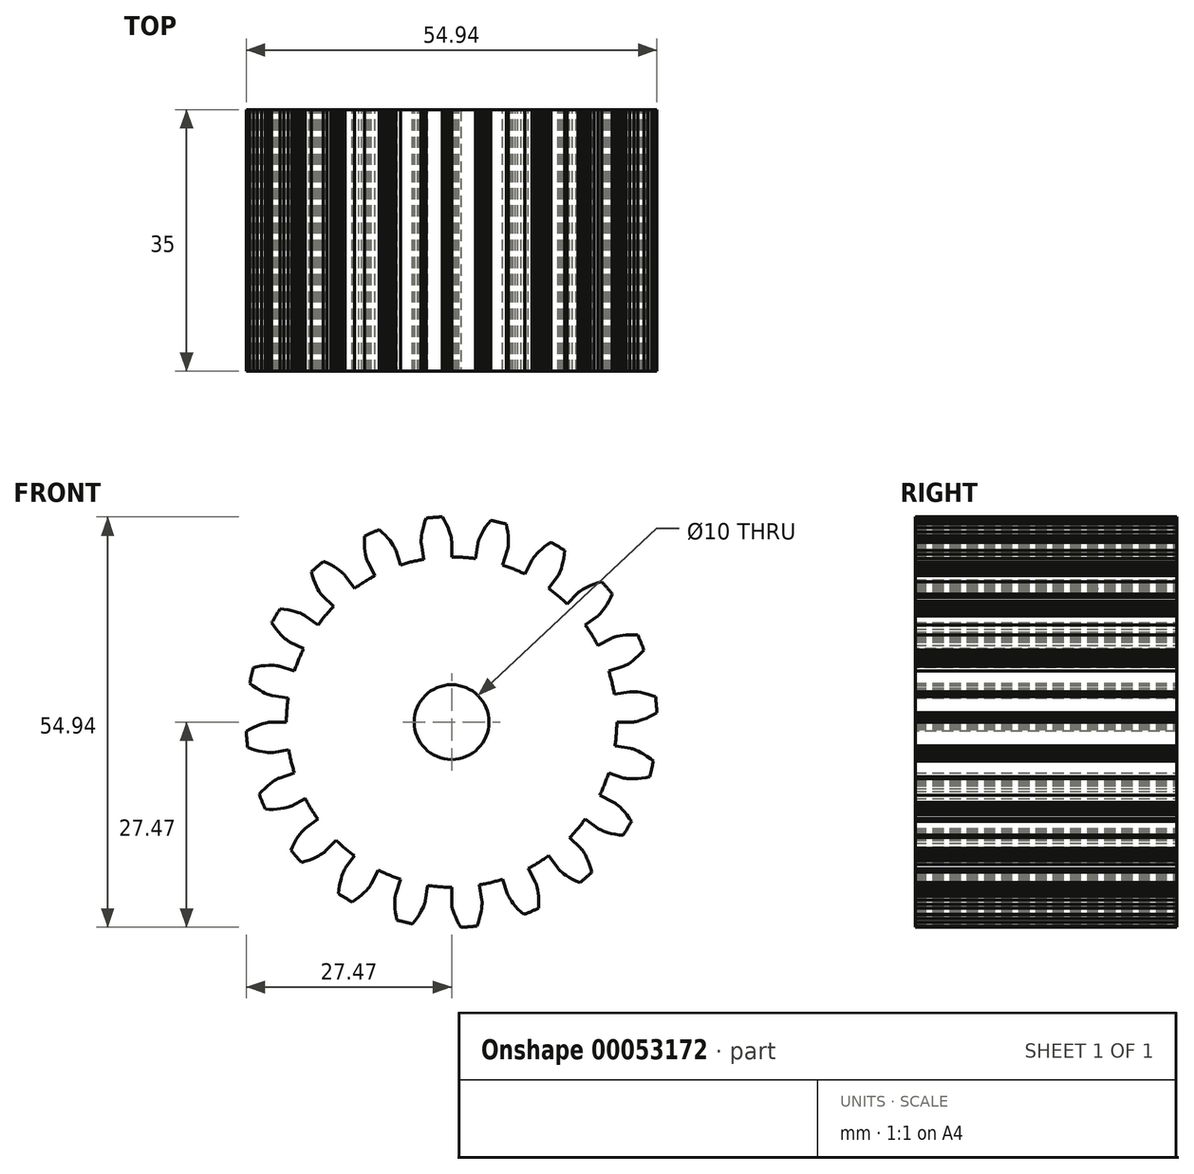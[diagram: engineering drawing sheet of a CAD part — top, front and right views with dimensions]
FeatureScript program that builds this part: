
annotation { "Feature Type Name" : "Feature", "Feature Type Description" : "" }
export const myFeature = defineFeature(function(context is Context, id is Id, definition is map)
    precondition{}
    {
        {
            var Q0;
            Q0=qCreatedBy(makeId("Front.planeOp"),FACE);
            var sketch = newSketch(context, id + "F0", { "sketchPlane" : qUnion([Q0])});
            skLineSegment(sketch, "E0", {"start": v(-24.2, 0) * mm, "end": v(-24.23, 0) * mm});
            skLineSegment(sketch, "E1", {"start": v(-24.23, 0) * mm, "end": v(-24.32, 0) * mm});
            skLineSegment(sketch, "E2", {"start": v(-24.32, 0) * mm, "end": v(-24.47, -0.03) * mm});
            skLineSegment(sketch, "E3", {"start": v(-24.47, -0.03) * mm, "end": v(-24.68, -0.06) * mm});
            skLineSegment(sketch, "E4", {"start": v(-24.68, -0.06) * mm, "end": v(-24.94, -0.13) * mm});
            skLineSegment(sketch, "E5", {"start": v(-24.94, -0.13) * mm, "end": v(-25.26, -0.22) * mm});
            skLineSegment(sketch, "E6", {"start": v(-25.26, -0.22) * mm, "end": v(-25.64, -0.34) * mm});
            skLineSegment(sketch, "E7", {"start": v(-25.64, -0.34) * mm, "end": v(-26.06, -0.5) * mm});
            skLineSegment(sketch, "E8", {"start": v(-26.06, -0.5) * mm, "end": v(-26.53, -0.72) * mm});
            skLineSegment(sketch, "E9", {"start": v(-26.53, -0.72) * mm, "end": v(-27.04, -0.98) * mm});
            skLineSegment(sketch, "E10", {"start": v(-27.04, -0.98) * mm, "end": v(-27.47, -1.24) * mm});
            skLineSegment(sketch, "E11", {"start": v(-23.86, -4.06) * mm, "end": v(-23.89, -4.06) * mm});
            skLineSegment(sketch, "E12", {"start": v(-23.89, -4.06) * mm, "end": v(-23.98, -4.07) * mm});
            skLineSegment(sketch, "E13", {"start": v(-23.98, -4.07) * mm, "end": v(-24.13, -4.07) * mm});
            skLineSegment(sketch, "E14", {"start": v(-24.13, -4.07) * mm, "end": v(-24.34, -4.07) * mm});
            skLineSegment(sketch, "E15", {"start": v(-24.34, -4.07) * mm, "end": v(-24.61, -4.06) * mm});
            skLineSegment(sketch, "E16", {"start": v(-24.61, -4.06) * mm, "end": v(-24.94, -4.02) * mm});
            skLineSegment(sketch, "E17", {"start": v(-24.94, -4.02) * mm, "end": v(-25.33, -3.96) * mm});
            skLineSegment(sketch, "E18", {"start": v(-25.33, -3.96) * mm, "end": v(-25.78, -3.87) * mm});
            skLineSegment(sketch, "E19", {"start": v(-25.78, -3.87) * mm, "end": v(-26.27, -3.73) * mm});
            skLineSegment(sketch, "E20", {"start": v(-26.27, -3.73) * mm, "end": v(-26.82, -3.56) * mm});
            skLineSegment(sketch, "E21", {"start": v(-26.82, -3.56) * mm, "end": v(-27.3, -3.39) * mm});
            skLineSegment(sketch, "E22", {"start": v(-23.86, -4.06) * mm, "end": v(-21.8, -3.7) * mm});
            skLineSegment(sketch, "E23", {"start": v(-24.2, 0) * mm, "end": v(-22.1, 0) * mm});
            skArc(sketch, "E24", {"start": v(-27.47, -1.24) * mm, "mid": v(-27.4, -2.31) * mm, "end": v(-27.3, -3.39) * mm});
            skLineSegment(sketch, "E25", {"start": v(-23.02, -7.48) * mm, "end": v(-23.04, -7.49) * mm});
            skLineSegment(sketch, "E26", {"start": v(-23.04, -7.49) * mm, "end": v(-23.13, -7.52) * mm});
            skLineSegment(sketch, "E27", {"start": v(-23.13, -7.52) * mm, "end": v(-23.26, -7.59) * mm});
            skLineSegment(sketch, "E28", {"start": v(-23.26, -7.59) * mm, "end": v(-23.45, -7.69) * mm});
            skLineSegment(sketch, "E29", {"start": v(-23.45, -7.69) * mm, "end": v(-23.68, -7.83) * mm});
            skLineSegment(sketch, "E30", {"start": v(-23.68, -7.83) * mm, "end": v(-23.96, -8.01) * mm});
            skLineSegment(sketch, "E31", {"start": v(-23.96, -8.01) * mm, "end": v(-24.28, -8.25) * mm});
            skLineSegment(sketch, "E32", {"start": v(-24.28, -8.25) * mm, "end": v(-24.63, -8.54) * mm});
            skLineSegment(sketch, "E33", {"start": v(-24.63, -8.54) * mm, "end": v(-25, -8.88) * mm});
            skLineSegment(sketch, "E34", {"start": v(-25, -8.88) * mm, "end": v(-25.41, -9.3) * mm});
            skLineSegment(sketch, "E35", {"start": v(-25.41, -9.3) * mm, "end": v(-25.75, -9.66) * mm});
            skLineSegment(sketch, "E36", {"start": v(-21.44, -11.23) * mm, "end": v(-21.46, -11.24) * mm});
            skLineSegment(sketch, "E37", {"start": v(-21.46, -11.24) * mm, "end": v(-21.55, -11.28) * mm});
            skLineSegment(sketch, "E38", {"start": v(-21.55, -11.28) * mm, "end": v(-21.69, -11.33) * mm});
            skLineSegment(sketch, "E39", {"start": v(-21.69, -11.33) * mm, "end": v(-21.9, -11.4) * mm});
            skLineSegment(sketch, "E40", {"start": v(-21.9, -11.4) * mm, "end": v(-22.15, -11.46) * mm});
            skLineSegment(sketch, "E41", {"start": v(-22.15, -11.46) * mm, "end": v(-22.48, -11.53) * mm});
            skLineSegment(sketch, "E42", {"start": v(-22.48, -11.53) * mm, "end": v(-22.87, -11.6) * mm});
            skLineSegment(sketch, "E43", {"start": v(-22.87, -11.6) * mm, "end": v(-23.32, -11.64) * mm});
            skLineSegment(sketch, "E44", {"start": v(-23.32, -11.64) * mm, "end": v(-23.83, -11.67) * mm});
            skLineSegment(sketch, "E45", {"start": v(-23.83, -11.67) * mm, "end": v(-24.4, -11.67) * mm});
            skLineSegment(sketch, "E46", {"start": v(-24.4, -11.67) * mm, "end": v(-24.9, -11.65) * mm});
            skLineSegment(sketch, "E47", {"start": v(-21.44, -11.23) * mm, "end": v(-19.58, -10.26) * mm});
            skLineSegment(sketch, "E48", {"start": v(-23.02, -7.48) * mm, "end": v(-21.03, -6.83) * mm});
            skArc(sketch, "E49", {"start": v(-25.75, -9.66) * mm, "mid": v(-25.35, -10.67) * mm, "end": v(-24.9, -11.65) * mm});
            skLineSegment(sketch, "E50", {"start": v(-19.58, -14.22) * mm, "end": v(-19.6, -14.24) * mm});
            skLineSegment(sketch, "E51", {"start": v(-19.6, -14.24) * mm, "end": v(-19.67, -14.3) * mm});
            skLineSegment(sketch, "E52", {"start": v(-19.67, -14.3) * mm, "end": v(-19.78, -14.4) * mm});
            skLineSegment(sketch, "E53", {"start": v(-19.78, -14.4) * mm, "end": v(-19.93, -14.56) * mm});
            skLineSegment(sketch, "E54", {"start": v(-19.93, -14.56) * mm, "end": v(-20.1, -14.76) * mm});
            skLineSegment(sketch, "E55", {"start": v(-20.1, -14.76) * mm, "end": v(-20.31, -15.03) * mm});
            skLineSegment(sketch, "E56", {"start": v(-20.31, -15.03) * mm, "end": v(-20.54, -15.35) * mm});
            skLineSegment(sketch, "E57", {"start": v(-20.54, -15.35) * mm, "end": v(-20.78, -15.73) * mm});
            skLineSegment(sketch, "E58", {"start": v(-20.78, -15.73) * mm, "end": v(-21.04, -16.18) * mm});
            skLineSegment(sketch, "E59", {"start": v(-21.04, -16.18) * mm, "end": v(-21.3, -16.69) * mm});
            skLineSegment(sketch, "E60", {"start": v(-21.3, -16.69) * mm, "end": v(-21.5, -17.15) * mm});
            skLineSegment(sketch, "E61", {"start": v(-16.92, -17.3) * mm, "end": v(-16.94, -17.33) * mm});
            skLineSegment(sketch, "E62", {"start": v(-16.94, -17.33) * mm, "end": v(-17, -17.38) * mm});
            skLineSegment(sketch, "E63", {"start": v(-17, -17.38) * mm, "end": v(-17.13, -17.48) * mm});
            skLineSegment(sketch, "E64", {"start": v(-17.13, -17.48) * mm, "end": v(-17.3, -17.6) * mm});
            skLineSegment(sketch, "E65", {"start": v(-17.3, -17.6) * mm, "end": v(-17.53, -17.75) * mm});
            skLineSegment(sketch, "E66", {"start": v(-17.53, -17.75) * mm, "end": v(-17.82, -17.91) * mm});
            skLineSegment(sketch, "E67", {"start": v(-17.82, -17.91) * mm, "end": v(-18.17, -18.1) * mm});
            skLineSegment(sketch, "E68", {"start": v(-18.17, -18.1) * mm, "end": v(-18.58, -18.28) * mm});
            skLineSegment(sketch, "E69", {"start": v(-18.58, -18.28) * mm, "end": v(-19.06, -18.46) * mm});
            skLineSegment(sketch, "E70", {"start": v(-19.06, -18.46) * mm, "end": v(-19.6, -18.65) * mm});
            skLineSegment(sketch, "E71", {"start": v(-19.6, -18.65) * mm, "end": v(-20.09, -18.78) * mm});
            skLineSegment(sketch, "E72", {"start": v(-16.92, -17.3) * mm, "end": v(-15.45, -15.8) * mm});
            skLineSegment(sketch, "E73", {"start": v(-19.58, -14.22) * mm, "end": v(-17.89, -13) * mm});
            skArc(sketch, "E74", {"start": v(-21.5, -17.15) * mm, "mid": v(-20.8, -17.98) * mm, "end": v(-20.09, -18.78) * mm});
            skLineSegment(sketch, "E75", {"start": v(-14.22, -19.58) * mm, "end": v(-14.24, -19.6) * mm});
            skLineSegment(sketch, "E76", {"start": v(-14.24, -19.6) * mm, "end": v(-14.29, -19.68) * mm});
            skLineSegment(sketch, "E77", {"start": v(-14.29, -19.68) * mm, "end": v(-14.36, -19.81) * mm});
            skLineSegment(sketch, "E78", {"start": v(-14.36, -19.81) * mm, "end": v(-14.45, -20) * mm});
            skLineSegment(sketch, "E79", {"start": v(-14.45, -20) * mm, "end": v(-14.56, -20.25) * mm});
            skLineSegment(sketch, "E80", {"start": v(-14.56, -20.25) * mm, "end": v(-14.68, -20.57) * mm});
            skLineSegment(sketch, "E81", {"start": v(-14.68, -20.57) * mm, "end": v(-14.8, -20.94) * mm});
            skLineSegment(sketch, "E82", {"start": v(-14.8, -20.94) * mm, "end": v(-14.9, -21.38) * mm});
            skLineSegment(sketch, "E83", {"start": v(-14.9, -21.38) * mm, "end": v(-15, -21.89) * mm});
            skLineSegment(sketch, "E84", {"start": v(-15, -21.89) * mm, "end": v(-15.1, -22.45) * mm});
            skLineSegment(sketch, "E85", {"start": v(-15.1, -22.45) * mm, "end": v(-15.15, -22.95) * mm});
            skLineSegment(sketch, "E86", {"start": v(-10.74, -21.69) * mm, "end": v(-10.76, -21.71) * mm});
            skLineSegment(sketch, "E87", {"start": v(-10.76, -21.71) * mm, "end": v(-10.8, -21.79) * mm});
            skLineSegment(sketch, "E88", {"start": v(-10.8, -21.79) * mm, "end": v(-10.89, -21.92) * mm});
            skLineSegment(sketch, "E89", {"start": v(-10.89, -21.92) * mm, "end": v(-11.01, -22.09) * mm});
            skLineSegment(sketch, "E90", {"start": v(-11.01, -22.09) * mm, "end": v(-11.19, -22.3) * mm});
            skLineSegment(sketch, "E91", {"start": v(-11.19, -22.3) * mm, "end": v(-11.4, -22.54) * mm});
            skLineSegment(sketch, "E92", {"start": v(-11.4, -22.54) * mm, "end": v(-11.69, -22.82) * mm});
            skLineSegment(sketch, "E93", {"start": v(-11.69, -22.82) * mm, "end": v(-12.02, -23.13) * mm});
            skLineSegment(sketch, "E94", {"start": v(-12.02, -23.13) * mm, "end": v(-12.42, -23.45) * mm});
            skLineSegment(sketch, "E95", {"start": v(-12.42, -23.45) * mm, "end": v(-12.88, -23.8) * mm});
            skLineSegment(sketch, "E96", {"start": v(-12.88, -23.8) * mm, "end": v(-13.3, -24.07) * mm});
            skLineSegment(sketch, "E97", {"start": v(-10.74, -21.69) * mm, "end": v(-9.81, -19.81) * mm});
            skLineSegment(sketch, "E98", {"start": v(-14.22, -19.58) * mm, "end": v(-13, -17.89) * mm});
            skArc(sketch, "E99", {"start": v(-15.15, -22.95) * mm, "mid": v(-14.24, -23.53) * mm, "end": v(-13.3, -24.07) * mm});
            skLineSegment(sketch, "E100", {"start": v(-7.48, -23.02) * mm, "end": v(-7.49, -23.04) * mm});
            skLineSegment(sketch, "E101", {"start": v(-7.49, -23.04) * mm, "end": v(-7.5, -23.13) * mm});
            skLineSegment(sketch, "E102", {"start": v(-7.5, -23.13) * mm, "end": v(-7.54, -23.28) * mm});
            skLineSegment(sketch, "E103", {"start": v(-7.54, -23.28) * mm, "end": v(-7.56, -23.5) * mm});
            skLineSegment(sketch, "E104", {"start": v(-7.56, -23.5) * mm, "end": v(-7.59, -23.76) * mm});
            skLineSegment(sketch, "E105", {"start": v(-7.59, -23.76) * mm, "end": v(-7.6, -24.1) * mm});
            skLineSegment(sketch, "E106", {"start": v(-7.6, -24.1) * mm, "end": v(-7.6, -24.49) * mm});
            skLineSegment(sketch, "E107", {"start": v(-7.6, -24.49) * mm, "end": v(-7.57, -24.94) * mm});
            skLineSegment(sketch, "E108", {"start": v(-7.57, -24.94) * mm, "end": v(-7.51, -25.45) * mm});
            skLineSegment(sketch, "E109", {"start": v(-7.51, -25.45) * mm, "end": v(-7.42, -26.02) * mm});
            skLineSegment(sketch, "E110", {"start": v(-7.42, -26.02) * mm, "end": v(-7.31, -26.5) * mm});
            skLineSegment(sketch, "E111", {"start": v(-3.52, -23.94) * mm, "end": v(-3.52, -23.97) * mm});
            skLineSegment(sketch, "E112", {"start": v(-3.52, -23.97) * mm, "end": v(-3.54, -24.06) * mm});
            skLineSegment(sketch, "E113", {"start": v(-3.54, -24.06) * mm, "end": v(-3.58, -24.2) * mm});
            skLineSegment(sketch, "E114", {"start": v(-3.58, -24.2) * mm, "end": v(-3.65, -24.4) * mm});
            skLineSegment(sketch, "E115", {"start": v(-3.65, -24.4) * mm, "end": v(-3.75, -24.66) * mm});
            skLineSegment(sketch, "E116", {"start": v(-3.75, -24.66) * mm, "end": v(-3.88, -24.97) * mm});
            skLineSegment(sketch, "E117", {"start": v(-3.88, -24.97) * mm, "end": v(-4.06, -25.32) * mm});
            skLineSegment(sketch, "E118", {"start": v(-4.06, -25.32) * mm, "end": v(-4.29, -25.7) * mm});
            skLineSegment(sketch, "E119", {"start": v(-4.29, -25.7) * mm, "end": v(-4.57, -26.14) * mm});
            skLineSegment(sketch, "E120", {"start": v(-4.57, -26.14) * mm, "end": v(-4.9, -26.6) * mm});
            skLineSegment(sketch, "E121", {"start": v(-4.9, -26.6) * mm, "end": v(-5.21, -27) * mm});
            skLineSegment(sketch, "E122", {"start": v(-3.52, -23.94) * mm, "end": v(-3.21, -21.87) * mm});
            skLineSegment(sketch, "E123", {"start": v(-7.48, -23.02) * mm, "end": v(-6.83, -21.03) * mm});
            skArc(sketch, "E124", {"start": v(-7.31, -26.5) * mm, "mid": v(-6.27, -26.78) * mm, "end": v(-5.21, -27) * mm});
            skLineSegment(sketch, "E125", {"start": v(0, -24.2) * mm, "end": v(0, -24.23) * mm});
            skLineSegment(sketch, "E126", {"start": v(0, -24.23) * mm, "end": v(0, -24.32) * mm});
            skLineSegment(sketch, "E127", {"start": v(0, -24.32) * mm, "end": v(0.03, -24.47) * mm});
            skLineSegment(sketch, "E128", {"start": v(0.03, -24.47) * mm, "end": v(0.06, -24.68) * mm});
            skLineSegment(sketch, "E129", {"start": v(0.06, -24.68) * mm, "end": v(0.13, -24.94) * mm});
            skLineSegment(sketch, "E130", {"start": v(0.13, -24.94) * mm, "end": v(0.22, -25.26) * mm});
            skLineSegment(sketch, "E131", {"start": v(0.22, -25.26) * mm, "end": v(0.34, -25.64) * mm});
            skLineSegment(sketch, "E132", {"start": v(0.34, -25.64) * mm, "end": v(0.5, -26.06) * mm});
            skLineSegment(sketch, "E133", {"start": v(0.5, -26.06) * mm, "end": v(0.72, -26.53) * mm});
            skLineSegment(sketch, "E134", {"start": v(0.72, -26.53) * mm, "end": v(0.98, -27.04) * mm});
            skLineSegment(sketch, "E135", {"start": v(0.98, -27.04) * mm, "end": v(1.24, -27.47) * mm});
            skLineSegment(sketch, "E136", {"start": v(4.06, -23.86) * mm, "end": v(4.06, -23.89) * mm});
            skLineSegment(sketch, "E137", {"start": v(4.06, -23.89) * mm, "end": v(4.07, -23.98) * mm});
            skLineSegment(sketch, "E138", {"start": v(4.07, -23.98) * mm, "end": v(4.07, -24.13) * mm});
            skLineSegment(sketch, "E139", {"start": v(4.07, -24.13) * mm, "end": v(4.07, -24.34) * mm});
            skLineSegment(sketch, "E140", {"start": v(4.07, -24.34) * mm, "end": v(4.06, -24.61) * mm});
            skLineSegment(sketch, "E141", {"start": v(4.06, -24.61) * mm, "end": v(4.02, -24.94) * mm});
            skLineSegment(sketch, "E142", {"start": v(4.02, -24.94) * mm, "end": v(3.96, -25.33) * mm});
            skLineSegment(sketch, "E143", {"start": v(3.96, -25.33) * mm, "end": v(3.87, -25.78) * mm});
            skLineSegment(sketch, "E144", {"start": v(3.87, -25.78) * mm, "end": v(3.73, -26.27) * mm});
            skLineSegment(sketch, "E145", {"start": v(3.73, -26.27) * mm, "end": v(3.56, -26.82) * mm});
            skLineSegment(sketch, "E146", {"start": v(3.56, -26.82) * mm, "end": v(3.39, -27.3) * mm});
            skLineSegment(sketch, "E147", {"start": v(4.06, -23.86) * mm, "end": v(3.7, -21.8) * mm});
            skLineSegment(sketch, "E148", {"start": v(0, -24.2) * mm, "end": v(0, -22.1) * mm});
            skArc(sketch, "E149", {"start": v(1.24, -27.47) * mm, "mid": v(2.31, -27.4) * mm, "end": v(3.39, -27.3) * mm});
            skLineSegment(sketch, "E150", {"start": v(7.48, -23.02) * mm, "end": v(7.49, -23.04) * mm});
            skLineSegment(sketch, "E151", {"start": v(7.49, -23.04) * mm, "end": v(7.52, -23.13) * mm});
            skLineSegment(sketch, "E152", {"start": v(7.52, -23.13) * mm, "end": v(7.59, -23.26) * mm});
            skLineSegment(sketch, "E153", {"start": v(7.59, -23.26) * mm, "end": v(7.69, -23.45) * mm});
            skLineSegment(sketch, "E154", {"start": v(7.69, -23.45) * mm, "end": v(7.83, -23.68) * mm});
            skLineSegment(sketch, "E155", {"start": v(7.83, -23.68) * mm, "end": v(8.01, -23.96) * mm});
            skLineSegment(sketch, "E156", {"start": v(8.01, -23.96) * mm, "end": v(8.25, -24.28) * mm});
            skLineSegment(sketch, "E157", {"start": v(8.25, -24.28) * mm, "end": v(8.54, -24.63) * mm});
            skLineSegment(sketch, "E158", {"start": v(8.54, -24.63) * mm, "end": v(8.88, -25) * mm});
            skLineSegment(sketch, "E159", {"start": v(8.88, -25) * mm, "end": v(9.3, -25.41) * mm});
            skLineSegment(sketch, "E160", {"start": v(9.3, -25.41) * mm, "end": v(9.66, -25.75) * mm});
            skLineSegment(sketch, "E161", {"start": v(11.23, -21.44) * mm, "end": v(11.24, -21.46) * mm});
            skLineSegment(sketch, "E162", {"start": v(11.24, -21.46) * mm, "end": v(11.28, -21.55) * mm});
            skLineSegment(sketch, "E163", {"start": v(11.28, -21.55) * mm, "end": v(11.33, -21.69) * mm});
            skLineSegment(sketch, "E164", {"start": v(11.33, -21.69) * mm, "end": v(11.4, -21.9) * mm});
            skLineSegment(sketch, "E165", {"start": v(11.4, -21.9) * mm, "end": v(11.46, -22.15) * mm});
            skLineSegment(sketch, "E166", {"start": v(11.46, -22.15) * mm, "end": v(11.53, -22.48) * mm});
            skLineSegment(sketch, "E167", {"start": v(11.53, -22.48) * mm, "end": v(11.6, -22.87) * mm});
            skLineSegment(sketch, "E168", {"start": v(11.6, -22.87) * mm, "end": v(11.64, -23.32) * mm});
            skLineSegment(sketch, "E169", {"start": v(11.64, -23.32) * mm, "end": v(11.67, -23.83) * mm});
            skLineSegment(sketch, "E170", {"start": v(11.67, -23.83) * mm, "end": v(11.67, -24.4) * mm});
            skLineSegment(sketch, "E171", {"start": v(11.67, -24.4) * mm, "end": v(11.65, -24.9) * mm});
            skLineSegment(sketch, "E172", {"start": v(11.23, -21.44) * mm, "end": v(10.26, -19.58) * mm});
            skLineSegment(sketch, "E173", {"start": v(7.48, -23.02) * mm, "end": v(6.83, -21.03) * mm});
            skArc(sketch, "E174", {"start": v(9.66, -25.75) * mm, "mid": v(10.67, -25.35) * mm, "end": v(11.65, -24.9) * mm});
            skLineSegment(sketch, "E175", {"start": v(14.22, -19.58) * mm, "end": v(14.24, -19.6) * mm});
            skLineSegment(sketch, "E176", {"start": v(14.24, -19.6) * mm, "end": v(14.3, -19.67) * mm});
            skLineSegment(sketch, "E177", {"start": v(14.3, -19.67) * mm, "end": v(14.4, -19.78) * mm});
            skLineSegment(sketch, "E178", {"start": v(14.4, -19.78) * mm, "end": v(14.56, -19.93) * mm});
            skLineSegment(sketch, "E179", {"start": v(14.56, -19.93) * mm, "end": v(14.76, -20.1) * mm});
            skLineSegment(sketch, "E180", {"start": v(14.76, -20.1) * mm, "end": v(15.03, -20.31) * mm});
            skLineSegment(sketch, "E181", {"start": v(15.03, -20.31) * mm, "end": v(15.35, -20.54) * mm});
            skLineSegment(sketch, "E182", {"start": v(15.35, -20.54) * mm, "end": v(15.73, -20.78) * mm});
            skLineSegment(sketch, "E183", {"start": v(15.73, -20.78) * mm, "end": v(16.18, -21.04) * mm});
            skLineSegment(sketch, "E184", {"start": v(16.18, -21.04) * mm, "end": v(16.69, -21.3) * mm});
            skLineSegment(sketch, "E185", {"start": v(16.69, -21.3) * mm, "end": v(17.15, -21.5) * mm});
            skLineSegment(sketch, "E186", {"start": v(17.3, -16.92) * mm, "end": v(17.33, -16.94) * mm});
            skLineSegment(sketch, "E187", {"start": v(17.33, -16.94) * mm, "end": v(17.38, -17) * mm});
            skLineSegment(sketch, "E188", {"start": v(17.38, -17) * mm, "end": v(17.48, -17.13) * mm});
            skLineSegment(sketch, "E189", {"start": v(17.48, -17.13) * mm, "end": v(17.6, -17.3) * mm});
            skLineSegment(sketch, "E190", {"start": v(17.6, -17.3) * mm, "end": v(17.75, -17.53) * mm});
            skLineSegment(sketch, "E191", {"start": v(17.75, -17.53) * mm, "end": v(17.91, -17.82) * mm});
            skLineSegment(sketch, "E192", {"start": v(17.91, -17.82) * mm, "end": v(18.1, -18.17) * mm});
            skLineSegment(sketch, "E193", {"start": v(18.1, -18.17) * mm, "end": v(18.28, -18.58) * mm});
            skLineSegment(sketch, "E194", {"start": v(18.28, -18.58) * mm, "end": v(18.46, -19.06) * mm});
            skLineSegment(sketch, "E195", {"start": v(18.46, -19.06) * mm, "end": v(18.65, -19.6) * mm});
            skLineSegment(sketch, "E196", {"start": v(18.65, -19.6) * mm, "end": v(18.78, -20.09) * mm});
            skLineSegment(sketch, "E197", {"start": v(17.3, -16.92) * mm, "end": v(15.8, -15.45) * mm});
            skLineSegment(sketch, "E198", {"start": v(14.22, -19.58) * mm, "end": v(13, -17.89) * mm});
            skArc(sketch, "E199", {"start": v(17.15, -21.5) * mm, "mid": v(17.98, -20.8) * mm, "end": v(18.78, -20.09) * mm});
            skLineSegment(sketch, "E200", {"start": v(19.58, -14.22) * mm, "end": v(19.6, -14.24) * mm});
            skLineSegment(sketch, "E201", {"start": v(19.6, -14.24) * mm, "end": v(19.68, -14.29) * mm});
            skLineSegment(sketch, "E202", {"start": v(19.68, -14.29) * mm, "end": v(19.81, -14.36) * mm});
            skLineSegment(sketch, "E203", {"start": v(19.81, -14.36) * mm, "end": v(20, -14.45) * mm});
            skLineSegment(sketch, "E204", {"start": v(20, -14.45) * mm, "end": v(20.25, -14.56) * mm});
            skLineSegment(sketch, "E205", {"start": v(20.25, -14.56) * mm, "end": v(20.57, -14.68) * mm});
            skLineSegment(sketch, "E206", {"start": v(20.57, -14.68) * mm, "end": v(20.94, -14.8) * mm});
            skLineSegment(sketch, "E207", {"start": v(20.94, -14.8) * mm, "end": v(21.38, -14.9) * mm});
            skLineSegment(sketch, "E208", {"start": v(21.38, -14.9) * mm, "end": v(21.89, -15) * mm});
            skLineSegment(sketch, "E209", {"start": v(21.89, -15) * mm, "end": v(22.45, -15.1) * mm});
            skLineSegment(sketch, "E210", {"start": v(22.45, -15.1) * mm, "end": v(22.95, -15.15) * mm});
            skLineSegment(sketch, "E211", {"start": v(21.69, -10.74) * mm, "end": v(21.71, -10.76) * mm});
            skLineSegment(sketch, "E212", {"start": v(21.71, -10.76) * mm, "end": v(21.79, -10.8) * mm});
            skLineSegment(sketch, "E213", {"start": v(21.79, -10.8) * mm, "end": v(21.92, -10.89) * mm});
            skLineSegment(sketch, "E214", {"start": v(21.92, -10.89) * mm, "end": v(22.09, -11.01) * mm});
            skLineSegment(sketch, "E215", {"start": v(22.09, -11.01) * mm, "end": v(22.3, -11.19) * mm});
            skLineSegment(sketch, "E216", {"start": v(22.3, -11.19) * mm, "end": v(22.54, -11.4) * mm});
            skLineSegment(sketch, "E217", {"start": v(22.54, -11.4) * mm, "end": v(22.82, -11.69) * mm});
            skLineSegment(sketch, "E218", {"start": v(22.82, -11.69) * mm, "end": v(23.13, -12.02) * mm});
            skLineSegment(sketch, "E219", {"start": v(23.13, -12.02) * mm, "end": v(23.45, -12.42) * mm});
            skLineSegment(sketch, "E220", {"start": v(23.45, -12.42) * mm, "end": v(23.8, -12.88) * mm});
            skLineSegment(sketch, "E221", {"start": v(23.8, -12.88) * mm, "end": v(24.07, -13.3) * mm});
            skLineSegment(sketch, "E222", {"start": v(21.69, -10.74) * mm, "end": v(19.81, -9.81) * mm});
            skLineSegment(sketch, "E223", {"start": v(19.58, -14.22) * mm, "end": v(17.89, -13) * mm});
            skArc(sketch, "E224", {"start": v(22.95, -15.15) * mm, "mid": v(23.53, -14.24) * mm, "end": v(24.07, -13.3) * mm});
            skLineSegment(sketch, "E225", {"start": v(23.02, -7.48) * mm, "end": v(23.04, -7.49) * mm});
            skLineSegment(sketch, "E226", {"start": v(23.04, -7.49) * mm, "end": v(23.13, -7.5) * mm});
            skLineSegment(sketch, "E227", {"start": v(23.13, -7.5) * mm, "end": v(23.28, -7.54) * mm});
            skLineSegment(sketch, "E228", {"start": v(23.28, -7.54) * mm, "end": v(23.5, -7.56) * mm});
            skLineSegment(sketch, "E229", {"start": v(23.5, -7.56) * mm, "end": v(23.76, -7.59) * mm});
            skLineSegment(sketch, "E230", {"start": v(23.76, -7.59) * mm, "end": v(24.1, -7.6) * mm});
            skLineSegment(sketch, "E231", {"start": v(24.1, -7.6) * mm, "end": v(24.49, -7.6) * mm});
            skLineSegment(sketch, "E232", {"start": v(24.49, -7.6) * mm, "end": v(24.94, -7.57) * mm});
            skLineSegment(sketch, "E233", {"start": v(24.94, -7.57) * mm, "end": v(25.45, -7.51) * mm});
            skLineSegment(sketch, "E234", {"start": v(25.45, -7.51) * mm, "end": v(26.02, -7.42) * mm});
            skLineSegment(sketch, "E235", {"start": v(26.02, -7.42) * mm, "end": v(26.5, -7.31) * mm});
            skLineSegment(sketch, "E236", {"start": v(23.94, -3.52) * mm, "end": v(23.97, -3.52) * mm});
            skLineSegment(sketch, "E237", {"start": v(23.97, -3.52) * mm, "end": v(24.06, -3.54) * mm});
            skLineSegment(sketch, "E238", {"start": v(24.06, -3.54) * mm, "end": v(24.2, -3.58) * mm});
            skLineSegment(sketch, "E239", {"start": v(24.2, -3.58) * mm, "end": v(24.4, -3.65) * mm});
            skLineSegment(sketch, "E240", {"start": v(24.4, -3.65) * mm, "end": v(24.66, -3.75) * mm});
            skLineSegment(sketch, "E241", {"start": v(24.66, -3.75) * mm, "end": v(24.97, -3.88) * mm});
            skLineSegment(sketch, "E242", {"start": v(24.97, -3.88) * mm, "end": v(25.32, -4.06) * mm});
            skLineSegment(sketch, "E243", {"start": v(25.32, -4.06) * mm, "end": v(25.7, -4.29) * mm});
            skLineSegment(sketch, "E244", {"start": v(25.7, -4.29) * mm, "end": v(26.14, -4.57) * mm});
            skLineSegment(sketch, "E245", {"start": v(26.14, -4.57) * mm, "end": v(26.6, -4.9) * mm});
            skLineSegment(sketch, "E246", {"start": v(26.6, -4.9) * mm, "end": v(27, -5.21) * mm});
            skLineSegment(sketch, "E247", {"start": v(23.94, -3.52) * mm, "end": v(21.87, -3.21) * mm});
            skLineSegment(sketch, "E248", {"start": v(23.02, -7.48) * mm, "end": v(21.03, -6.83) * mm});
            skArc(sketch, "E249", {"start": v(26.5, -7.31) * mm, "mid": v(26.78, -6.27) * mm, "end": v(27, -5.21) * mm});
            skLineSegment(sketch, "E250", {"start": v(24.2, 0) * mm, "end": v(24.23, 0) * mm});
            skLineSegment(sketch, "E251", {"start": v(24.23, 0) * mm, "end": v(24.32, 0) * mm});
            skLineSegment(sketch, "E252", {"start": v(24.32, 0) * mm, "end": v(24.47, 0.03) * mm});
            skLineSegment(sketch, "E253", {"start": v(24.47, 0.03) * mm, "end": v(24.68, 0.06) * mm});
            skLineSegment(sketch, "E254", {"start": v(24.68, 0.06) * mm, "end": v(24.94, 0.13) * mm});
            skLineSegment(sketch, "E255", {"start": v(24.94, 0.13) * mm, "end": v(25.26, 0.22) * mm});
            skLineSegment(sketch, "E256", {"start": v(25.26, 0.22) * mm, "end": v(25.64, 0.34) * mm});
            skLineSegment(sketch, "E257", {"start": v(25.64, 0.34) * mm, "end": v(26.06, 0.5) * mm});
            skLineSegment(sketch, "E258", {"start": v(26.06, 0.5) * mm, "end": v(26.53, 0.72) * mm});
            skLineSegment(sketch, "E259", {"start": v(26.53, 0.72) * mm, "end": v(27.04, 0.98) * mm});
            skLineSegment(sketch, "E260", {"start": v(27.04, 0.98) * mm, "end": v(27.47, 1.24) * mm});
            skLineSegment(sketch, "E261", {"start": v(23.86, 4.06) * mm, "end": v(23.89, 4.06) * mm});
            skLineSegment(sketch, "E262", {"start": v(23.89, 4.06) * mm, "end": v(23.98, 4.07) * mm});
            skLineSegment(sketch, "E263", {"start": v(23.98, 4.07) * mm, "end": v(24.13, 4.07) * mm});
            skLineSegment(sketch, "E264", {"start": v(24.13, 4.07) * mm, "end": v(24.34, 4.07) * mm});
            skLineSegment(sketch, "E265", {"start": v(24.34, 4.07) * mm, "end": v(24.61, 4.06) * mm});
            skLineSegment(sketch, "E266", {"start": v(24.61, 4.06) * mm, "end": v(24.94, 4.02) * mm});
            skLineSegment(sketch, "E267", {"start": v(24.94, 4.02) * mm, "end": v(25.33, 3.96) * mm});
            skLineSegment(sketch, "E268", {"start": v(25.33, 3.96) * mm, "end": v(25.78, 3.87) * mm});
            skLineSegment(sketch, "E269", {"start": v(25.78, 3.87) * mm, "end": v(26.27, 3.73) * mm});
            skLineSegment(sketch, "E270", {"start": v(26.27, 3.73) * mm, "end": v(26.82, 3.56) * mm});
            skLineSegment(sketch, "E271", {"start": v(26.82, 3.56) * mm, "end": v(27.3, 3.39) * mm});
            skLineSegment(sketch, "E272", {"start": v(23.86, 4.06) * mm, "end": v(21.8, 3.7) * mm});
            skLineSegment(sketch, "E273", {"start": v(24.2, 0) * mm, "end": v(22.1, 0) * mm});
            skArc(sketch, "E274", {"start": v(27.47, 1.24) * mm, "mid": v(27.4, 2.31) * mm, "end": v(27.3, 3.39) * mm});
            skLineSegment(sketch, "E275", {"start": v(23.02, 7.48) * mm, "end": v(23.04, 7.49) * mm});
            skLineSegment(sketch, "E276", {"start": v(23.04, 7.49) * mm, "end": v(23.13, 7.52) * mm});
            skLineSegment(sketch, "E277", {"start": v(23.13, 7.52) * mm, "end": v(23.26, 7.59) * mm});
            skLineSegment(sketch, "E278", {"start": v(23.26, 7.59) * mm, "end": v(23.45, 7.69) * mm});
            skLineSegment(sketch, "E279", {"start": v(23.45, 7.69) * mm, "end": v(23.68, 7.83) * mm});
            skLineSegment(sketch, "E280", {"start": v(23.68, 7.83) * mm, "end": v(23.96, 8.01) * mm});
            skLineSegment(sketch, "E281", {"start": v(23.96, 8.01) * mm, "end": v(24.28, 8.25) * mm});
            skLineSegment(sketch, "E282", {"start": v(24.28, 8.25) * mm, "end": v(24.63, 8.54) * mm});
            skLineSegment(sketch, "E283", {"start": v(24.63, 8.54) * mm, "end": v(25, 8.88) * mm});
            skLineSegment(sketch, "E284", {"start": v(25, 8.88) * mm, "end": v(25.41, 9.3) * mm});
            skLineSegment(sketch, "E285", {"start": v(25.41, 9.3) * mm, "end": v(25.75, 9.66) * mm});
            skLineSegment(sketch, "E286", {"start": v(21.44, 11.23) * mm, "end": v(21.46, 11.24) * mm});
            skLineSegment(sketch, "E287", {"start": v(21.46, 11.24) * mm, "end": v(21.55, 11.28) * mm});
            skLineSegment(sketch, "E288", {"start": v(21.55, 11.28) * mm, "end": v(21.69, 11.33) * mm});
            skLineSegment(sketch, "E289", {"start": v(21.69, 11.33) * mm, "end": v(21.9, 11.4) * mm});
            skLineSegment(sketch, "E290", {"start": v(21.9, 11.4) * mm, "end": v(22.15, 11.46) * mm});
            skLineSegment(sketch, "E291", {"start": v(22.15, 11.46) * mm, "end": v(22.48, 11.53) * mm});
            skLineSegment(sketch, "E292", {"start": v(22.48, 11.53) * mm, "end": v(22.87, 11.6) * mm});
            skLineSegment(sketch, "E293", {"start": v(22.87, 11.6) * mm, "end": v(23.32, 11.64) * mm});
            skLineSegment(sketch, "E294", {"start": v(23.32, 11.64) * mm, "end": v(23.83, 11.67) * mm});
            skLineSegment(sketch, "E295", {"start": v(23.83, 11.67) * mm, "end": v(24.4, 11.67) * mm});
            skLineSegment(sketch, "E296", {"start": v(24.4, 11.67) * mm, "end": v(24.9, 11.65) * mm});
            skLineSegment(sketch, "E297", {"start": v(21.44, 11.23) * mm, "end": v(19.58, 10.26) * mm});
            skLineSegment(sketch, "E298", {"start": v(23.02, 7.48) * mm, "end": v(21.03, 6.83) * mm});
            skArc(sketch, "E299", {"start": v(25.75, 9.66) * mm, "mid": v(25.35, 10.67) * mm, "end": v(24.9, 11.65) * mm});
            skLineSegment(sketch, "E300", {"start": v(19.58, 14.22) * mm, "end": v(19.6, 14.24) * mm});
            skLineSegment(sketch, "E301", {"start": v(19.6, 14.24) * mm, "end": v(19.67, 14.3) * mm});
            skLineSegment(sketch, "E302", {"start": v(19.67, 14.3) * mm, "end": v(19.78, 14.4) * mm});
            skLineSegment(sketch, "E303", {"start": v(19.78, 14.4) * mm, "end": v(19.93, 14.56) * mm});
            skLineSegment(sketch, "E304", {"start": v(19.93, 14.56) * mm, "end": v(20.1, 14.76) * mm});
            skLineSegment(sketch, "E305", {"start": v(20.1, 14.76) * mm, "end": v(20.31, 15.03) * mm});
            skLineSegment(sketch, "E306", {"start": v(20.31, 15.03) * mm, "end": v(20.54, 15.35) * mm});
            skLineSegment(sketch, "E307", {"start": v(20.54, 15.35) * mm, "end": v(20.78, 15.73) * mm});
            skLineSegment(sketch, "E308", {"start": v(20.78, 15.73) * mm, "end": v(21.04, 16.18) * mm});
            skLineSegment(sketch, "E309", {"start": v(21.04, 16.18) * mm, "end": v(21.3, 16.69) * mm});
            skLineSegment(sketch, "E310", {"start": v(21.3, 16.69) * mm, "end": v(21.5, 17.15) * mm});
            skLineSegment(sketch, "E311", {"start": v(16.92, 17.3) * mm, "end": v(16.94, 17.33) * mm});
            skLineSegment(sketch, "E312", {"start": v(16.94, 17.33) * mm, "end": v(17, 17.38) * mm});
            skLineSegment(sketch, "E313", {"start": v(17, 17.38) * mm, "end": v(17.13, 17.48) * mm});
            skLineSegment(sketch, "E314", {"start": v(17.13, 17.48) * mm, "end": v(17.3, 17.6) * mm});
            skLineSegment(sketch, "E315", {"start": v(17.3, 17.6) * mm, "end": v(17.53, 17.75) * mm});
            skLineSegment(sketch, "E316", {"start": v(17.53, 17.75) * mm, "end": v(17.82, 17.91) * mm});
            skLineSegment(sketch, "E317", {"start": v(17.82, 17.91) * mm, "end": v(18.17, 18.1) * mm});
            skLineSegment(sketch, "E318", {"start": v(18.17, 18.1) * mm, "end": v(18.58, 18.28) * mm});
            skLineSegment(sketch, "E319", {"start": v(18.58, 18.28) * mm, "end": v(19.06, 18.46) * mm});
            skLineSegment(sketch, "E320", {"start": v(19.06, 18.46) * mm, "end": v(19.6, 18.65) * mm});
            skLineSegment(sketch, "E321", {"start": v(19.6, 18.65) * mm, "end": v(20.09, 18.78) * mm});
            skLineSegment(sketch, "E322", {"start": v(16.92, 17.3) * mm, "end": v(15.45, 15.8) * mm});
            skLineSegment(sketch, "E323", {"start": v(19.58, 14.22) * mm, "end": v(17.89, 13) * mm});
            skArc(sketch, "E324", {"start": v(21.5, 17.15) * mm, "mid": v(20.8, 17.98) * mm, "end": v(20.09, 18.78) * mm});
            skLineSegment(sketch, "E325", {"start": v(14.22, 19.58) * mm, "end": v(14.24, 19.6) * mm});
            skLineSegment(sketch, "E326", {"start": v(14.24, 19.6) * mm, "end": v(14.29, 19.68) * mm});
            skLineSegment(sketch, "E327", {"start": v(14.29, 19.68) * mm, "end": v(14.36, 19.81) * mm});
            skLineSegment(sketch, "E328", {"start": v(14.36, 19.81) * mm, "end": v(14.45, 20) * mm});
            skLineSegment(sketch, "E329", {"start": v(14.45, 20) * mm, "end": v(14.56, 20.25) * mm});
            skLineSegment(sketch, "E330", {"start": v(14.56, 20.25) * mm, "end": v(14.68, 20.57) * mm});
            skLineSegment(sketch, "E331", {"start": v(14.68, 20.57) * mm, "end": v(14.8, 20.94) * mm});
            skLineSegment(sketch, "E332", {"start": v(14.8, 20.94) * mm, "end": v(14.9, 21.38) * mm});
            skLineSegment(sketch, "E333", {"start": v(14.9, 21.38) * mm, "end": v(15, 21.89) * mm});
            skLineSegment(sketch, "E334", {"start": v(15, 21.89) * mm, "end": v(15.1, 22.45) * mm});
            skLineSegment(sketch, "E335", {"start": v(15.1, 22.45) * mm, "end": v(15.15, 22.95) * mm});
            skLineSegment(sketch, "E336", {"start": v(10.74, 21.69) * mm, "end": v(10.76, 21.71) * mm});
            skLineSegment(sketch, "E337", {"start": v(10.76, 21.71) * mm, "end": v(10.8, 21.79) * mm});
            skLineSegment(sketch, "E338", {"start": v(10.8, 21.79) * mm, "end": v(10.89, 21.92) * mm});
            skLineSegment(sketch, "E339", {"start": v(10.89, 21.92) * mm, "end": v(11.01, 22.09) * mm});
            skLineSegment(sketch, "E340", {"start": v(11.01, 22.09) * mm, "end": v(11.19, 22.3) * mm});
            skLineSegment(sketch, "E341", {"start": v(11.19, 22.3) * mm, "end": v(11.4, 22.54) * mm});
            skLineSegment(sketch, "E342", {"start": v(11.4, 22.54) * mm, "end": v(11.69, 22.82) * mm});
            skLineSegment(sketch, "E343", {"start": v(11.69, 22.82) * mm, "end": v(12.02, 23.13) * mm});
            skLineSegment(sketch, "E344", {"start": v(12.02, 23.13) * mm, "end": v(12.42, 23.45) * mm});
            skLineSegment(sketch, "E345", {"start": v(12.42, 23.45) * mm, "end": v(12.88, 23.8) * mm});
            skLineSegment(sketch, "E346", {"start": v(12.88, 23.8) * mm, "end": v(13.3, 24.07) * mm});
            skLineSegment(sketch, "E347", {"start": v(10.74, 21.69) * mm, "end": v(9.81, 19.81) * mm});
            skLineSegment(sketch, "E348", {"start": v(14.22, 19.58) * mm, "end": v(13, 17.89) * mm});
            skArc(sketch, "E349", {"start": v(15.15, 22.95) * mm, "mid": v(14.24, 23.53) * mm, "end": v(13.3, 24.07) * mm});
            skLineSegment(sketch, "E350", {"start": v(7.48, 23.02) * mm, "end": v(7.49, 23.04) * mm});
            skLineSegment(sketch, "E351", {"start": v(7.49, 23.04) * mm, "end": v(7.5, 23.13) * mm});
            skLineSegment(sketch, "E352", {"start": v(7.5, 23.13) * mm, "end": v(7.54, 23.28) * mm});
            skLineSegment(sketch, "E353", {"start": v(7.54, 23.28) * mm, "end": v(7.56, 23.5) * mm});
            skLineSegment(sketch, "E354", {"start": v(7.56, 23.5) * mm, "end": v(7.59, 23.76) * mm});
            skLineSegment(sketch, "E355", {"start": v(7.59, 23.76) * mm, "end": v(7.6, 24.1) * mm});
            skLineSegment(sketch, "E356", {"start": v(7.6, 24.1) * mm, "end": v(7.6, 24.49) * mm});
            skLineSegment(sketch, "E357", {"start": v(7.6, 24.49) * mm, "end": v(7.57, 24.94) * mm});
            skLineSegment(sketch, "E358", {"start": v(7.57, 24.94) * mm, "end": v(7.51, 25.45) * mm});
            skLineSegment(sketch, "E359", {"start": v(7.51, 25.45) * mm, "end": v(7.42, 26.02) * mm});
            skLineSegment(sketch, "E360", {"start": v(7.42, 26.02) * mm, "end": v(7.31, 26.5) * mm});
            skLineSegment(sketch, "E361", {"start": v(3.52, 23.94) * mm, "end": v(3.52, 23.97) * mm});
            skLineSegment(sketch, "E362", {"start": v(3.52, 23.97) * mm, "end": v(3.54, 24.06) * mm});
            skLineSegment(sketch, "E363", {"start": v(3.54, 24.06) * mm, "end": v(3.58, 24.2) * mm});
            skLineSegment(sketch, "E364", {"start": v(3.58, 24.2) * mm, "end": v(3.65, 24.4) * mm});
            skLineSegment(sketch, "E365", {"start": v(3.65, 24.4) * mm, "end": v(3.75, 24.66) * mm});
            skLineSegment(sketch, "E366", {"start": v(3.75, 24.66) * mm, "end": v(3.88, 24.97) * mm});
            skLineSegment(sketch, "E367", {"start": v(3.88, 24.97) * mm, "end": v(4.06, 25.32) * mm});
            skLineSegment(sketch, "E368", {"start": v(4.06, 25.32) * mm, "end": v(4.29, 25.7) * mm});
            skLineSegment(sketch, "E369", {"start": v(4.29, 25.7) * mm, "end": v(4.57, 26.14) * mm});
            skLineSegment(sketch, "E370", {"start": v(4.57, 26.14) * mm, "end": v(4.9, 26.6) * mm});
            skLineSegment(sketch, "E371", {"start": v(4.9, 26.6) * mm, "end": v(5.21, 27) * mm});
            skLineSegment(sketch, "E372", {"start": v(3.52, 23.94) * mm, "end": v(3.21, 21.87) * mm});
            skLineSegment(sketch, "E373", {"start": v(7.48, 23.02) * mm, "end": v(6.83, 21.03) * mm});
            skArc(sketch, "E374", {"start": v(7.31, 26.5) * mm, "mid": v(6.27, 26.78) * mm, "end": v(5.21, 27) * mm});
            skLineSegment(sketch, "E375", {"start": v(0, 24.2) * mm, "end": v(0, 24.23) * mm});
            skLineSegment(sketch, "E376", {"start": v(0, 24.23) * mm, "end": v(0, 24.32) * mm});
            skLineSegment(sketch, "E377", {"start": v(0, 24.32) * mm, "end": v(-0.03, 24.47) * mm});
            skLineSegment(sketch, "E378", {"start": v(-0.03, 24.47) * mm, "end": v(-0.06, 24.68) * mm});
            skLineSegment(sketch, "E379", {"start": v(-0.06, 24.68) * mm, "end": v(-0.13, 24.94) * mm});
            skLineSegment(sketch, "E380", {"start": v(-0.13, 24.94) * mm, "end": v(-0.22, 25.26) * mm});
            skLineSegment(sketch, "E381", {"start": v(-0.22, 25.26) * mm, "end": v(-0.34, 25.64) * mm});
            skLineSegment(sketch, "E382", {"start": v(-0.34, 25.64) * mm, "end": v(-0.5, 26.06) * mm});
            skLineSegment(sketch, "E383", {"start": v(-0.5, 26.06) * mm, "end": v(-0.72, 26.53) * mm});
            skLineSegment(sketch, "E384", {"start": v(-0.72, 26.53) * mm, "end": v(-0.98, 27.04) * mm});
            skLineSegment(sketch, "E385", {"start": v(-0.98, 27.04) * mm, "end": v(-1.24, 27.47) * mm});
            skLineSegment(sketch, "E386", {"start": v(-4.06, 23.86) * mm, "end": v(-4.06, 23.89) * mm});
            skLineSegment(sketch, "E387", {"start": v(-4.06, 23.89) * mm, "end": v(-4.07, 23.98) * mm});
            skLineSegment(sketch, "E388", {"start": v(-4.07, 23.98) * mm, "end": v(-4.07, 24.13) * mm});
            skLineSegment(sketch, "E389", {"start": v(-4.07, 24.13) * mm, "end": v(-4.07, 24.34) * mm});
            skLineSegment(sketch, "E390", {"start": v(-4.07, 24.34) * mm, "end": v(-4.06, 24.61) * mm});
            skLineSegment(sketch, "E391", {"start": v(-4.06, 24.61) * mm, "end": v(-4.02, 24.94) * mm});
            skLineSegment(sketch, "E392", {"start": v(-4.02, 24.94) * mm, "end": v(-3.96, 25.33) * mm});
            skLineSegment(sketch, "E393", {"start": v(-3.96, 25.33) * mm, "end": v(-3.87, 25.78) * mm});
            skLineSegment(sketch, "E394", {"start": v(-3.87, 25.78) * mm, "end": v(-3.73, 26.27) * mm});
            skLineSegment(sketch, "E395", {"start": v(-3.73, 26.27) * mm, "end": v(-3.56, 26.82) * mm});
            skLineSegment(sketch, "E396", {"start": v(-3.56, 26.82) * mm, "end": v(-3.39, 27.3) * mm});
            skLineSegment(sketch, "E397", {"start": v(-4.06, 23.86) * mm, "end": v(-3.7, 21.8) * mm});
            skLineSegment(sketch, "E398", {"start": v(0, 24.2) * mm, "end": v(0, 22.1) * mm});
            skArc(sketch, "E399", {"start": v(-1.24, 27.47) * mm, "mid": v(-2.31, 27.4) * mm, "end": v(-3.39, 27.3) * mm});
            skLineSegment(sketch, "E400", {"start": v(-7.48, 23.02) * mm, "end": v(-7.49, 23.04) * mm});
            skLineSegment(sketch, "E401", {"start": v(-7.49, 23.04) * mm, "end": v(-7.52, 23.13) * mm});
            skLineSegment(sketch, "E402", {"start": v(-7.52, 23.13) * mm, "end": v(-7.59, 23.26) * mm});
            skLineSegment(sketch, "E403", {"start": v(-7.59, 23.26) * mm, "end": v(-7.69, 23.45) * mm});
            skLineSegment(sketch, "E404", {"start": v(-7.69, 23.45) * mm, "end": v(-7.83, 23.68) * mm});
            skLineSegment(sketch, "E405", {"start": v(-7.83, 23.68) * mm, "end": v(-8.01, 23.96) * mm});
            skLineSegment(sketch, "E406", {"start": v(-8.01, 23.96) * mm, "end": v(-8.25, 24.28) * mm});
            skLineSegment(sketch, "E407", {"start": v(-8.25, 24.28) * mm, "end": v(-8.54, 24.63) * mm});
            skLineSegment(sketch, "E408", {"start": v(-8.54, 24.63) * mm, "end": v(-8.88, 25) * mm});
            skLineSegment(sketch, "E409", {"start": v(-8.88, 25) * mm, "end": v(-9.3, 25.41) * mm});
            skLineSegment(sketch, "E410", {"start": v(-9.3, 25.41) * mm, "end": v(-9.66, 25.75) * mm});
            skLineSegment(sketch, "E411", {"start": v(-11.23, 21.44) * mm, "end": v(-11.24, 21.46) * mm});
            skLineSegment(sketch, "E412", {"start": v(-11.24, 21.46) * mm, "end": v(-11.28, 21.55) * mm});
            skLineSegment(sketch, "E413", {"start": v(-11.28, 21.55) * mm, "end": v(-11.33, 21.69) * mm});
            skLineSegment(sketch, "E414", {"start": v(-11.33, 21.69) * mm, "end": v(-11.4, 21.9) * mm});
            skLineSegment(sketch, "E415", {"start": v(-11.4, 21.9) * mm, "end": v(-11.46, 22.15) * mm});
            skLineSegment(sketch, "E416", {"start": v(-11.46, 22.15) * mm, "end": v(-11.53, 22.48) * mm});
            skLineSegment(sketch, "E417", {"start": v(-11.53, 22.48) * mm, "end": v(-11.6, 22.87) * mm});
            skLineSegment(sketch, "E418", {"start": v(-11.6, 22.87) * mm, "end": v(-11.64, 23.32) * mm});
            skLineSegment(sketch, "E419", {"start": v(-11.64, 23.32) * mm, "end": v(-11.67, 23.83) * mm});
            skLineSegment(sketch, "E420", {"start": v(-11.67, 23.83) * mm, "end": v(-11.67, 24.4) * mm});
            skLineSegment(sketch, "E421", {"start": v(-11.67, 24.4) * mm, "end": v(-11.65, 24.9) * mm});
            skLineSegment(sketch, "E422", {"start": v(-11.23, 21.44) * mm, "end": v(-10.26, 19.58) * mm});
            skLineSegment(sketch, "E423", {"start": v(-7.48, 23.02) * mm, "end": v(-6.83, 21.03) * mm});
            skArc(sketch, "E424", {"start": v(-9.66, 25.75) * mm, "mid": v(-10.67, 25.35) * mm, "end": v(-11.65, 24.9) * mm});
            skLineSegment(sketch, "E425", {"start": v(-14.22, 19.58) * mm, "end": v(-14.24, 19.6) * mm});
            skLineSegment(sketch, "E426", {"start": v(-14.24, 19.6) * mm, "end": v(-14.3, 19.67) * mm});
            skLineSegment(sketch, "E427", {"start": v(-14.3, 19.67) * mm, "end": v(-14.4, 19.78) * mm});
            skLineSegment(sketch, "E428", {"start": v(-14.4, 19.78) * mm, "end": v(-14.56, 19.93) * mm});
            skLineSegment(sketch, "E429", {"start": v(-14.56, 19.93) * mm, "end": v(-14.76, 20.1) * mm});
            skLineSegment(sketch, "E430", {"start": v(-14.76, 20.1) * mm, "end": v(-15.03, 20.31) * mm});
            skLineSegment(sketch, "E431", {"start": v(-15.03, 20.31) * mm, "end": v(-15.35, 20.54) * mm});
            skLineSegment(sketch, "E432", {"start": v(-15.35, 20.54) * mm, "end": v(-15.73, 20.78) * mm});
            skLineSegment(sketch, "E433", {"start": v(-15.73, 20.78) * mm, "end": v(-16.18, 21.04) * mm});
            skLineSegment(sketch, "E434", {"start": v(-16.18, 21.04) * mm, "end": v(-16.69, 21.3) * mm});
            skLineSegment(sketch, "E435", {"start": v(-16.69, 21.3) * mm, "end": v(-17.15, 21.5) * mm});
            skLineSegment(sketch, "E436", {"start": v(-17.3, 16.92) * mm, "end": v(-17.33, 16.94) * mm});
            skLineSegment(sketch, "E437", {"start": v(-17.33, 16.94) * mm, "end": v(-17.38, 17) * mm});
            skLineSegment(sketch, "E438", {"start": v(-17.38, 17) * mm, "end": v(-17.48, 17.13) * mm});
            skLineSegment(sketch, "E439", {"start": v(-17.48, 17.13) * mm, "end": v(-17.6, 17.3) * mm});
            skLineSegment(sketch, "E440", {"start": v(-17.6, 17.3) * mm, "end": v(-17.75, 17.53) * mm});
            skLineSegment(sketch, "E441", {"start": v(-17.75, 17.53) * mm, "end": v(-17.91, 17.82) * mm});
            skLineSegment(sketch, "E442", {"start": v(-17.91, 17.82) * mm, "end": v(-18.1, 18.17) * mm});
            skLineSegment(sketch, "E443", {"start": v(-18.1, 18.17) * mm, "end": v(-18.28, 18.58) * mm});
            skLineSegment(sketch, "E444", {"start": v(-18.28, 18.58) * mm, "end": v(-18.46, 19.06) * mm});
            skLineSegment(sketch, "E445", {"start": v(-18.46, 19.06) * mm, "end": v(-18.65, 19.6) * mm});
            skLineSegment(sketch, "E446", {"start": v(-18.65, 19.6) * mm, "end": v(-18.78, 20.09) * mm});
            skLineSegment(sketch, "E447", {"start": v(-17.3, 16.92) * mm, "end": v(-15.8, 15.45) * mm});
            skLineSegment(sketch, "E448", {"start": v(-14.22, 19.58) * mm, "end": v(-13, 17.89) * mm});
            skArc(sketch, "E449", {"start": v(-17.15, 21.5) * mm, "mid": v(-17.98, 20.8) * mm, "end": v(-18.78, 20.09) * mm});
            skLineSegment(sketch, "E450", {"start": v(-19.58, 14.22) * mm, "end": v(-19.6, 14.24) * mm});
            skLineSegment(sketch, "E451", {"start": v(-19.6, 14.24) * mm, "end": v(-19.68, 14.29) * mm});
            skLineSegment(sketch, "E452", {"start": v(-19.68, 14.29) * mm, "end": v(-19.81, 14.36) * mm});
            skLineSegment(sketch, "E453", {"start": v(-19.81, 14.36) * mm, "end": v(-20, 14.45) * mm});
            skLineSegment(sketch, "E454", {"start": v(-20, 14.45) * mm, "end": v(-20.25, 14.56) * mm});
            skLineSegment(sketch, "E455", {"start": v(-20.25, 14.56) * mm, "end": v(-20.57, 14.68) * mm});
            skLineSegment(sketch, "E456", {"start": v(-20.57, 14.68) * mm, "end": v(-20.94, 14.8) * mm});
            skLineSegment(sketch, "E457", {"start": v(-20.94, 14.8) * mm, "end": v(-21.38, 14.9) * mm});
            skLineSegment(sketch, "E458", {"start": v(-21.38, 14.9) * mm, "end": v(-21.89, 15) * mm});
            skLineSegment(sketch, "E459", {"start": v(-21.89, 15) * mm, "end": v(-22.45, 15.1) * mm});
            skLineSegment(sketch, "E460", {"start": v(-22.45, 15.1) * mm, "end": v(-22.95, 15.15) * mm});
            skLineSegment(sketch, "E461", {"start": v(-21.69, 10.74) * mm, "end": v(-21.71, 10.76) * mm});
            skLineSegment(sketch, "E462", {"start": v(-21.71, 10.76) * mm, "end": v(-21.79, 10.8) * mm});
            skLineSegment(sketch, "E463", {"start": v(-21.79, 10.8) * mm, "end": v(-21.92, 10.89) * mm});
            skLineSegment(sketch, "E464", {"start": v(-21.92, 10.89) * mm, "end": v(-22.09, 11.01) * mm});
            skLineSegment(sketch, "E465", {"start": v(-22.09, 11.01) * mm, "end": v(-22.3, 11.19) * mm});
            skLineSegment(sketch, "E466", {"start": v(-22.3, 11.19) * mm, "end": v(-22.54, 11.4) * mm});
            skLineSegment(sketch, "E467", {"start": v(-22.54, 11.4) * mm, "end": v(-22.82, 11.69) * mm});
            skLineSegment(sketch, "E468", {"start": v(-22.82, 11.69) * mm, "end": v(-23.13, 12.02) * mm});
            skLineSegment(sketch, "E469", {"start": v(-23.13, 12.02) * mm, "end": v(-23.45, 12.42) * mm});
            skLineSegment(sketch, "E470", {"start": v(-23.45, 12.42) * mm, "end": v(-23.8, 12.88) * mm});
            skLineSegment(sketch, "E471", {"start": v(-23.8, 12.88) * mm, "end": v(-24.07, 13.3) * mm});
            skLineSegment(sketch, "E472", {"start": v(-21.69, 10.74) * mm, "end": v(-19.81, 9.81) * mm});
            skLineSegment(sketch, "E473", {"start": v(-19.58, 14.22) * mm, "end": v(-17.89, 13) * mm});
            skArc(sketch, "E474", {"start": v(-22.95, 15.15) * mm, "mid": v(-23.53, 14.24) * mm, "end": v(-24.07, 13.3) * mm});
            skLineSegment(sketch, "E475", {"start": v(-23.02, 7.48) * mm, "end": v(-23.04, 7.49) * mm});
            skLineSegment(sketch, "E476", {"start": v(-23.04, 7.49) * mm, "end": v(-23.13, 7.5) * mm});
            skLineSegment(sketch, "E477", {"start": v(-23.13, 7.5) * mm, "end": v(-23.28, 7.54) * mm});
            skLineSegment(sketch, "E478", {"start": v(-23.28, 7.54) * mm, "end": v(-23.5, 7.56) * mm});
            skLineSegment(sketch, "E479", {"start": v(-23.5, 7.56) * mm, "end": v(-23.76, 7.59) * mm});
            skLineSegment(sketch, "E480", {"start": v(-23.76, 7.59) * mm, "end": v(-24.1, 7.6) * mm});
            skLineSegment(sketch, "E481", {"start": v(-24.1, 7.6) * mm, "end": v(-24.49, 7.6) * mm});
            skLineSegment(sketch, "E482", {"start": v(-24.49, 7.6) * mm, "end": v(-24.94, 7.57) * mm});
            skLineSegment(sketch, "E483", {"start": v(-24.94, 7.57) * mm, "end": v(-25.45, 7.51) * mm});
            skLineSegment(sketch, "E484", {"start": v(-25.45, 7.51) * mm, "end": v(-26.02, 7.42) * mm});
            skLineSegment(sketch, "E485", {"start": v(-26.02, 7.42) * mm, "end": v(-26.5, 7.31) * mm});
            skLineSegment(sketch, "E486", {"start": v(-23.94, 3.52) * mm, "end": v(-23.97, 3.52) * mm});
            skLineSegment(sketch, "E487", {"start": v(-23.97, 3.52) * mm, "end": v(-24.06, 3.54) * mm});
            skLineSegment(sketch, "E488", {"start": v(-24.06, 3.54) * mm, "end": v(-24.2, 3.58) * mm});
            skLineSegment(sketch, "E489", {"start": v(-24.2, 3.58) * mm, "end": v(-24.4, 3.65) * mm});
            skLineSegment(sketch, "E490", {"start": v(-24.4, 3.65) * mm, "end": v(-24.66, 3.75) * mm});
            skLineSegment(sketch, "E491", {"start": v(-24.66, 3.75) * mm, "end": v(-24.97, 3.88) * mm});
            skLineSegment(sketch, "E492", {"start": v(-24.97, 3.88) * mm, "end": v(-25.32, 4.06) * mm});
            skLineSegment(sketch, "E493", {"start": v(-25.32, 4.06) * mm, "end": v(-25.7, 4.29) * mm});
            skLineSegment(sketch, "E494", {"start": v(-25.7, 4.29) * mm, "end": v(-26.14, 4.57) * mm});
            skLineSegment(sketch, "E495", {"start": v(-26.14, 4.57) * mm, "end": v(-26.6, 4.9) * mm});
            skLineSegment(sketch, "E496", {"start": v(-26.6, 4.9) * mm, "end": v(-27, 5.21) * mm});
            skLineSegment(sketch, "E497", {"start": v(-23.94, 3.52) * mm, "end": v(-21.87, 3.21) * mm});
            skLineSegment(sketch, "E498", {"start": v(-23.02, 7.48) * mm, "end": v(-21.03, 6.83) * mm});
            skArc(sketch, "E499", {"start": v(-26.5, 7.31) * mm, "mid": v(-26.78, 6.27) * mm, "end": v(-27, 5.21) * mm});
            skCircle(sketch, "E500", {"center": v(0, 0) * mm, "radius": 5 * mm});
            skArc(sketch, "E501", {"start": v(-19.81, 9.81) * mm, "mid": v(-20.47, 8.34) * mm, "end": v(-21.03, 6.83) * mm});
            skArc(sketch, "E502", {"start": v(-21.87, 3.21) * mm, "mid": v(-22.05, 1.6) * mm, "end": v(-22.1, 0) * mm});
            skArc(sketch, "E503", {"start": v(-21.8, -3.7) * mm, "mid": v(-21.47, -5.28) * mm, "end": v(-21.03, -6.83) * mm});
            skArc(sketch, "E504", {"start": v(-19.58, -10.26) * mm, "mid": v(-18.78, -11.66) * mm, "end": v(-17.89, -13) * mm});
            skArc(sketch, "E505", {"start": v(-15.45, -15.8) * mm, "mid": v(-14.26, -16.9) * mm, "end": v(-13, -17.89) * mm});
            skArc(sketch, "E506", {"start": v(-9.81, -19.81) * mm, "mid": v(-8.34, -20.47) * mm, "end": v(-6.83, -21.03) * mm});
            skArc(sketch, "E507", {"start": v(-3.21, -21.87) * mm, "mid": v(-1.6, -22.05) * mm, "end": v(0, -22.1) * mm});
            skArc(sketch, "E508", {"start": v(3.7, -21.8) * mm, "mid": v(5.28, -21.47) * mm, "end": v(6.83, -21.03) * mm});
            skArc(sketch, "E509", {"start": v(10.26, -19.58) * mm, "mid": v(11.66, -18.78) * mm, "end": v(13, -17.89) * mm});
            skArc(sketch, "E510", {"start": v(15.8, -15.45) * mm, "mid": v(16.9, -14.26) * mm, "end": v(17.89, -13) * mm});
            skArc(sketch, "E511", {"start": v(19.81, -9.81) * mm, "mid": v(20.47, -8.34) * mm, "end": v(21.03, -6.83) * mm});
            skArc(sketch, "E512", {"start": v(21.87, -3.21) * mm, "mid": v(22.05, -1.6) * mm, "end": v(22.1, 0) * mm});
            skArc(sketch, "E513", {"start": v(21.8, 3.7) * mm, "mid": v(21.47, 5.28) * mm, "end": v(21.03, 6.83) * mm});
            skArc(sketch, "E514", {"start": v(19.58, 10.26) * mm, "mid": v(18.78, 11.66) * mm, "end": v(17.89, 13) * mm});
            skArc(sketch, "E515", {"start": v(15.45, 15.8) * mm, "mid": v(14.26, 16.9) * mm, "end": v(13, 17.89) * mm});
            skArc(sketch, "E516", {"start": v(9.81, 19.81) * mm, "mid": v(8.34, 20.47) * mm, "end": v(6.83, 21.03) * mm});
            skArc(sketch, "E517", {"start": v(3.21, 21.87) * mm, "mid": v(1.6, 22.05) * mm, "end": v(0, 22.1) * mm});
            skArc(sketch, "E518", {"start": v(-3.7, 21.8) * mm, "mid": v(-5.28, 21.47) * mm, "end": v(-6.83, 21.03) * mm});
            skArc(sketch, "E519", {"start": v(-10.26, 19.58) * mm, "mid": v(-11.66, 18.78) * mm, "end": v(-13, 17.89) * mm});
            skArc(sketch, "E520", {"start": v(-15.8, 15.45) * mm, "mid": v(-16.9, 14.26) * mm, "end": v(-17.89, 13) * mm});
            skSolve(sketch);
        }
        {
            var Q0;
            Q0 = qSketchRegion(id + "F0", true);
            extrude(context, id + "F1", {"entities" : qUnion([Q0]), "depth" : 35 * mm});
        }
    });
